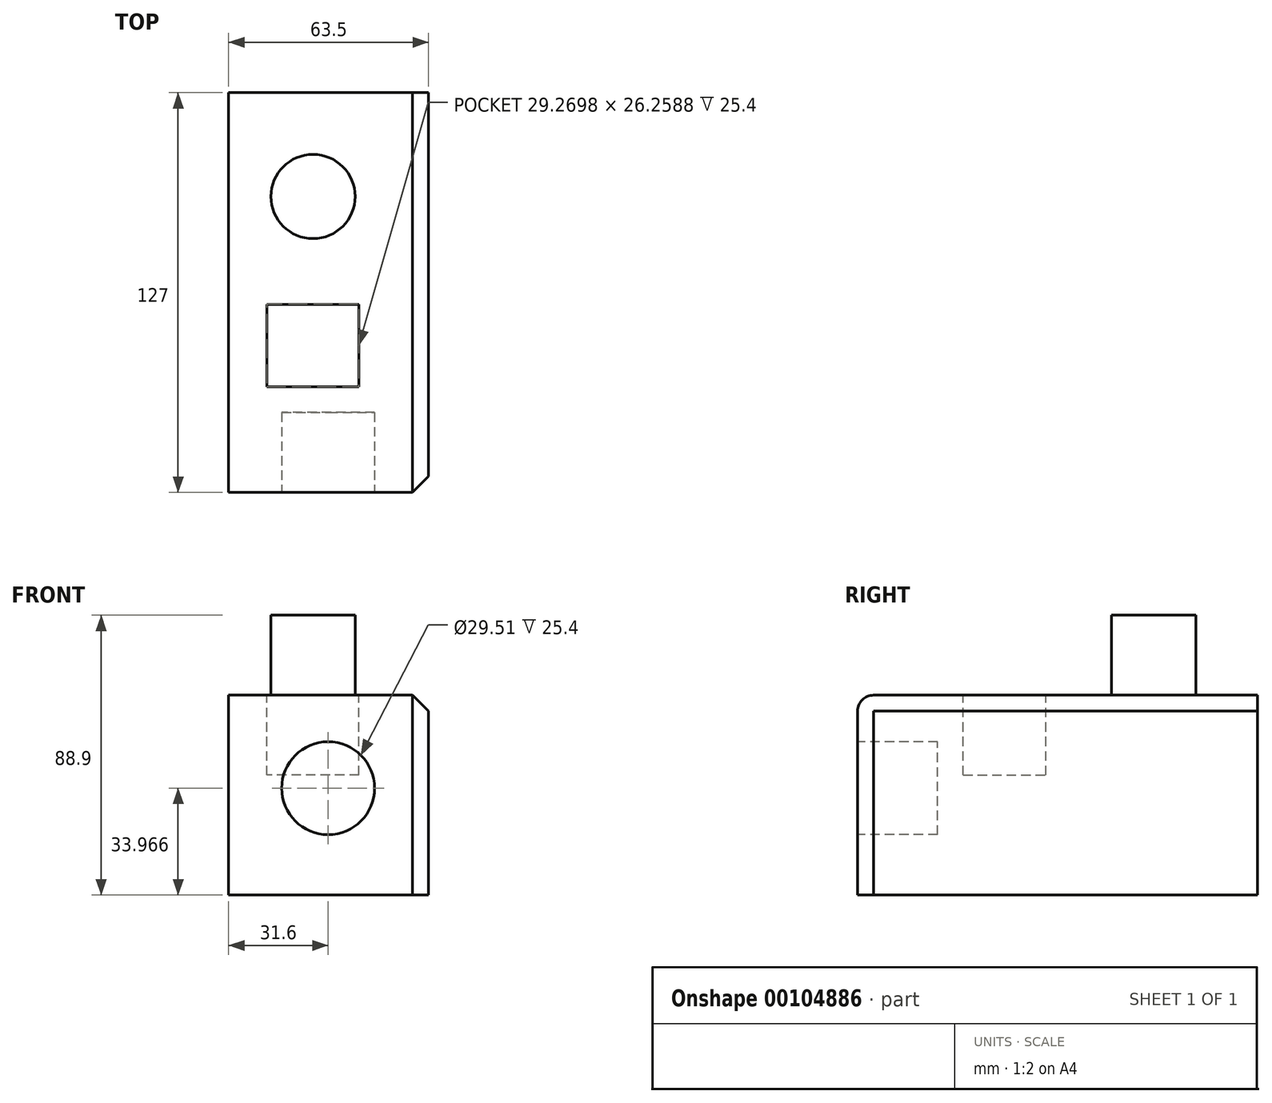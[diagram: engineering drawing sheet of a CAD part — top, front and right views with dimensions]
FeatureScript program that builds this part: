
annotation { "Feature Type Name" : "Feature", "Feature Type Description" : "" }
export const myFeature = defineFeature(function(context is Context, id is Id, definition is map)
    precondition{}
    {
        {
            var Q0;
            Q0=qCreatedBy(makeId("Front.planeOp"),FACE);
            var sketch = newSketch(context, id + "F0", { "sketchPlane" : qUnion([Q0])});
            skLineSegment(sketch, "E0.bottom", {"start": v(0, 0) * mm, "end": v(63.5, 0) * mm});
            skLineSegment(sketch, "E0.top", {"start": v(0, 63.5) * mm, "end": v(63.5, 63.5) * mm});
            skLineSegment(sketch, "E0.left", {"start": v(0, 0) * mm, "end": v(0, 63.5) * mm});
            skLineSegment(sketch, "E0.right", {"start": v(63.5, 0) * mm, "end": v(63.5, 63.5) * mm});
            skSolve(sketch);
        }
        {
            var Q0;
            Q0=makeQuery(id+"F0.imprint","IMPRINT",FACE,{"disambiguationData":[TD([[makeQuery(id+"F0.imprint","IMPRINT",EDGE,{"derivedFrom":sQuery(id+"F0.wireOp",EDGE,"E0.bottom")}),1.0]])]});
            extrude(context, id + "F1", {"entities" : qUnion([Q0]), "oppositeDirection" : true, "depth" : 127 * mm});
        }
        {
            var Q0;
            Q0=makeQuery(id+"F1.opExtrude","CAP_EDGE",EDGE,{"disambiguationData":[OSD([sQuery(id+"F0.wireOp",EDGE,"E0.top")])],"isStart":true});
            fillet(context, id + "F2", {"entities" : qUnion([Q0]), "radius" : 5.08 * mm, "tangentPropagation" : true, "allowEdgeOverflow" : false});
        }
        {
            var Q0;
            Q0=makeQuery(id+"F1.opExtrude","SWEPT_EDGE",EDGE,{"disambiguationData":[OSD([sQuery(id+"F0.wireOp",EDGE,"E0.top"),sQuery(id+"F0.wireOp",EDGE,"E0.right")])]});
            var Q1;
            Q1=makeQuery(id+"F1.opExtrude","CAP_EDGE",EDGE,{"disambiguationData":[OSD([sQuery(id+"F0.wireOp",EDGE,"E0.right")])],"isStart":true});
            chamfer(context, id + "F3", {"entities" : qUnion([Q0, Q1]), "width" : 5.08 * mm, "tangentPropagation" : true});
        }
        {
            var Q0;
            Q0=makeQuery(id+"F1.opExtrude","SWEPT_FACE",FACE,{"disambiguationData":[OSD([sQuery(id+"F0.wireOp",EDGE,"E0.top")])]});
            var sketch = newSketch(context, id + "F4", { "sketchPlane" : qUnion([Q0])});
            skCircle(sketch, "E1", {"center": v(26.79, 94) * mm, "radius": 13.37 * mm});
            skLineSegment(sketch, "E2.bottom", {"start": v(41.37, 33.53) * mm, "end": v(12.1, 33.53) * mm});
            skLineSegment(sketch, "E2.top", {"start": v(41.37, 59.8) * mm, "end": v(12.1, 59.8) * mm});
            skLineSegment(sketch, "E2.left", {"start": v(41.37, 33.53) * mm, "end": v(41.37, 59.8) * mm});
            skLineSegment(sketch, "E2.right", {"start": v(12.1, 33.53) * mm, "end": v(12.1, 59.8) * mm});
            skSolve(sketch);
        }
        {
            var Q0;
            Q0=makeQuery(id+"F4.imprint","IMPRINT",FACE,{"disambiguationData":[TD([[makeQuery(id+"F4.imprint","IMPRINT",EDGE,{"derivedFrom":sQuery(id+"F4.wireOp",EDGE,"E2.bottom")}),-1.0]])]});
            extrude(context, id + "F5", {"entities" : qUnion([Q0]), "operationType" : NewBodyOperationType.REMOVE, "oppositeDirection" : true, "depth" : 25.4 * mm});
        }
        {
            var Q0;
            Q0=makeQuery(id+"F4.imprint","IMPRINT",FACE,{"disambiguationData":[TD([[makeQuery(id+"F4.imprint","IMPRINT",EDGE,{"derivedFrom":sQuery(id+"F4.wireOp",EDGE,"E1")}),1.0]])]});
            extrude(context, id + "F6", {"entities" : qUnion([Q0]), "operationType" : NewBodyOperationType.ADD, "depth" : 25.4 * mm});
        }
        {
            var Q0;
            Q0=makeQuery(id+"F1.opExtrude","CAP_FACE",FACE,{"disambiguationData":[OSD([sQuery(id+"F0.wireOp",EDGE,"E0.bottom"),sQuery(id+"F0.wireOp",EDGE,"E0.top"),sQuery(id+"F0.wireOp",EDGE,"E0.left"),sQuery(id+"F0.wireOp",EDGE,"E0.right")])],"isStart":true});
            var sketch = newSketch(context, id + "F7", { "sketchPlane" : qUnion([Q0])});
            skCircle(sketch, "E3", {"center": v(31.6, 33.97) * mm, "radius": 14.76 * mm});
            skSolve(sketch);
        }
        {
            var Q0;
            Q0=makeQuery(id+"F7.imprint","IMPRINT",FACE,{"disambiguationData":[TD([[makeQuery(id+"F7.imprint","IMPRINT",EDGE,{"derivedFrom":sQuery(id+"F7.wireOp",EDGE,"E3")}),1.0]])]});
            extrude(context, id + "F8", {"entities" : qUnion([Q0]), "operationType" : NewBodyOperationType.REMOVE, "oppositeDirection" : true, "depth" : 25.4 * mm});
        }
    });
